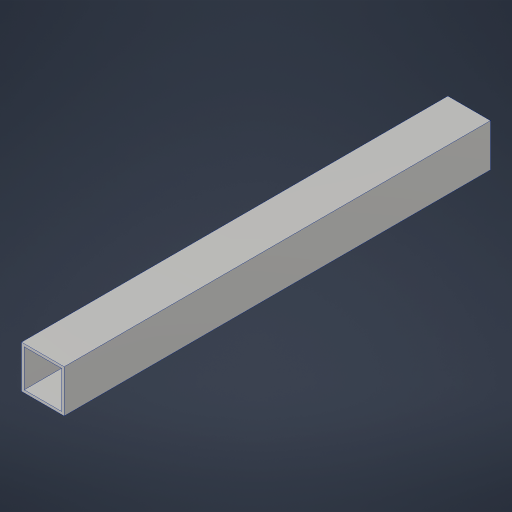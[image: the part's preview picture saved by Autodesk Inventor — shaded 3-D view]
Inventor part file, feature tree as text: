
AUTODESK INVENTOR PART (.ipt)
format: ipt  version: 2023.4 (Build 274418000, 418)  size: 167,936 bytes
history: native  units: in
note: dims shown in document units (in); Inventor stores cm internally (conversion verified against a paired STEP export)
features: extrude x1
ambient origin geometry x8: Origin, YZ Plane, XZ Plane, XY Plane, X Axis, Y Axis, Z Axis, Center Point
bodies: Solid1 (feature_tree)
feature tree (1):
  extrude  "Extrusion1"  TaperAngle=0.0deg  [1 undecoded]
note: 1 required parameter value undecoded (feature->parameter linkage not recoverable at this tier; creation-order binding heuristic only, values carry confidence <= 0.55)
